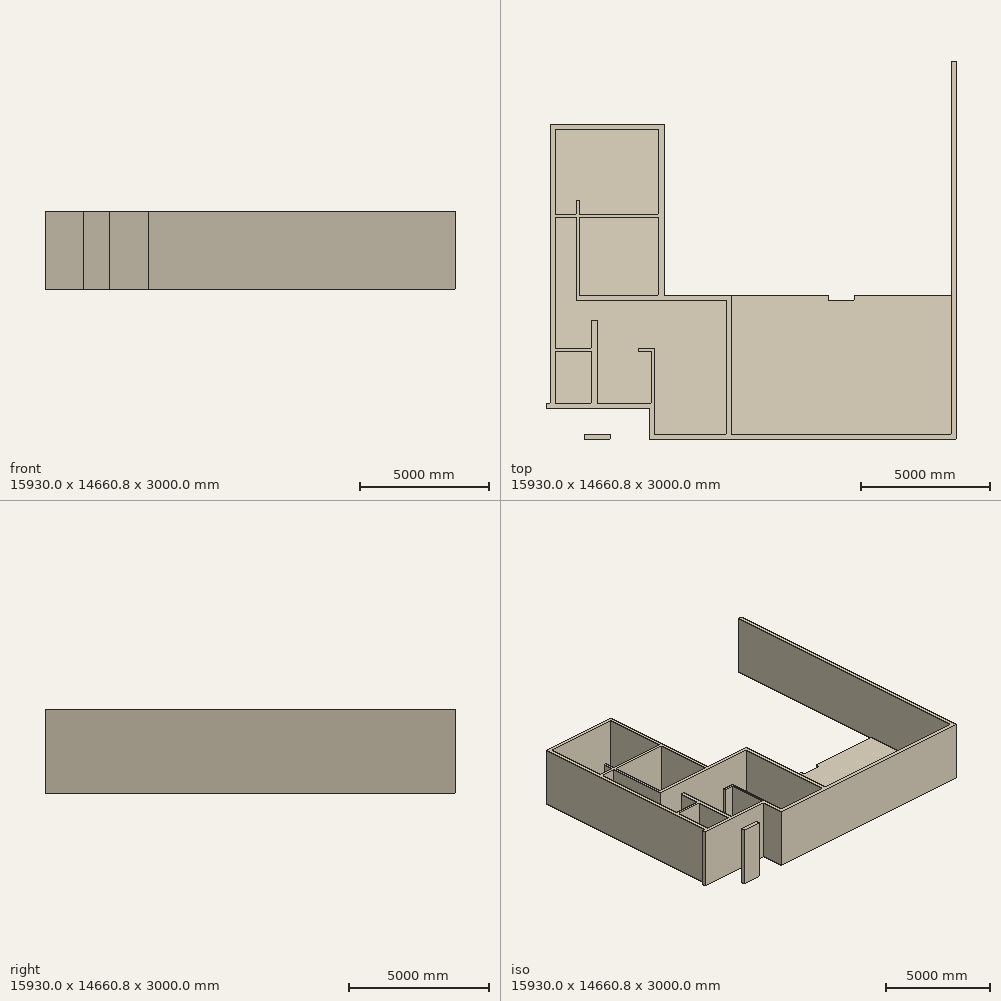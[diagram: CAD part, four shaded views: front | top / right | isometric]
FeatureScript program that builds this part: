
annotation { "Feature Type Name" : "Feature", "Feature Type Description" : "" }
export const myFeature = defineFeature(function(context is Context, id is Id, definition is map)
    precondition{}
    {
        {
            var Q0;
            Q0=qCreatedBy(makeId("Top.planeOp"),FACE);
            var sketch = newSketch(context, id + "F0", { "sketchPlane" : qUnion([Q0])});
            skLineSegment(sketch, "E0.bottom", {"start": v(-7965, 7850) * mm, "end": v(7965, 7850) * mm});
            skLineSegment(sketch, "E0.top", {"start": v(-7965, -7850) * mm, "end": v(7965, -7850) * mm});
            skLineSegment(sketch, "E0.left", {"start": v(-7965, 7850) * mm, "end": v(-7965, -7850) * mm});
            skLineSegment(sketch, "E0.right", {"start": v(7965, 7850) * mm, "end": v(7965, -7850) * mm});
            skSolve(sketch);
        }
        {
            var Q0;
            Q0=qCreatedBy(makeId("Top.planeOp"),FACE);
            var sketch = newSketch(context, id + "F1", { "sketchPlane" : qUnion([Q0])});
            skLineSegment(sketch, "E1", {"start": v(-7797.5, 5409.25) * mm, "end": v(-3397.5, 5409.25) * mm});
            skLineSegment(sketch, "E2", {"start": v(-3397.5, 5409.25) * mm, "end": v(-3397.5, -1210.75) * mm});
            skLineSegment(sketch, "E3", {"start": v(-3397.5, -1210.75) * mm, "end": v(-777.5, -1210.75) * mm});
            skLineSegment(sketch, "E4", {"start": v(-777.5, -1210.75) * mm, "end": v(-777.5, -6610.75) * mm});
            skLineSegment(sketch, "E5", {"start": v(7965, -6810.75) * mm, "end": v(-3977.5, -6810.75) * mm});
            skLineSegment(sketch, "E6", {"start": v(-3977.5, -6810.75) * mm, "end": v(-3977.5, -5610.75) * mm});
            skLineSegment(sketch, "E7", {"start": v(-3977.5, -5610.75) * mm, "end": v(-7437.94, -5610.75) * mm});
            skLineSegment(sketch, "E8", {"start": v(-7597.5, 5209.25) * mm, "end": v(-3597.5, 5209.25) * mm});
            skLineSegment(sketch, "E9", {"start": v(-3597.5, 5209.25) * mm, "end": v(-3597.5, 1909.25) * mm});
            skLineSegment(sketch, "E10", {"start": v(-3597.5, 1909.25) * mm, "end": v(-6697.5, 1909.25) * mm});
            skLineSegment(sketch, "E11", {"start": v(-6697.5, 1909.25) * mm, "end": v(-6697.5, 2459.25) * mm});
            skLineSegment(sketch, "E12", {"start": v(-6697.5, 2459.25) * mm, "end": v(-6817.5, 2459.25) * mm});
            skLineSegment(sketch, "E13", {"start": v(-6817.5, 2459.25) * mm, "end": v(-6817.5, 1909.25) * mm});
            skLineSegment(sketch, "E14", {"start": v(-6817.5, 1909.25) * mm, "end": v(-7597.5, 1909.25) * mm});
            skLineSegment(sketch, "E15", {"start": v(-7597.5, 1909.25) * mm, "end": v(-7597.5, 5209.25) * mm});
            skLineSegment(sketch, "E16.bottom", {"start": v(-6697.5, 1789.25) * mm, "end": v(-3597.5, 1789.25) * mm});
            skLineSegment(sketch, "E16.top", {"start": v(-6697.5, -1210.75) * mm, "end": v(-3597.5, -1210.75) * mm});
            skLineSegment(sketch, "E16.left", {"start": v(-6697.5, 1789.25) * mm, "end": v(-6697.5, -1210.75) * mm});
            skLineSegment(sketch, "E16.right", {"start": v(-3597.5, 1789.25) * mm, "end": v(-3597.5, -1210.75) * mm});
            skLineSegment(sketch, "E17", {"start": v(-7597.5, 1789.25) * mm, "end": v(-6817.5, 1789.25) * mm});
            skLineSegment(sketch, "E18", {"start": v(-6817.5, 1789.25) * mm, "end": v(-6817.5, -1410.75) * mm});
            skLineSegment(sketch, "E19", {"start": v(-6817.5, -1410.75) * mm, "end": v(-977.5, -1410.75) * mm});
            skLineSegment(sketch, "E20", {"start": v(-977.5, -1410.75) * mm, "end": v(-977.5, -6610.75) * mm});
            skLineSegment(sketch, "E21", {"start": v(-977.5, -6610.75) * mm, "end": v(-3777.5, -6610.75) * mm});
            skLineSegment(sketch, "E22", {"start": v(-3777.5, -6610.75) * mm, "end": v(-3777.5, -3290.75) * mm});
            skLineSegment(sketch, "E23", {"start": v(-3777.5, -3290.75) * mm, "end": v(-4397.5, -3290.75) * mm});
            skLineSegment(sketch, "E24", {"start": v(-4397.5, -3290.75) * mm, "end": v(-4397.5, -3410.75) * mm});
            skLineSegment(sketch, "E25", {"start": v(-4397.5, -3410.75) * mm, "end": v(-3897.5, -3410.75) * mm});
            skLineSegment(sketch, "E26", {"start": v(-3897.5, -3410.75) * mm, "end": v(-3897.5, -5410.75) * mm});
            skLineSegment(sketch, "E27", {"start": v(-3897.5, -5410.75) * mm, "end": v(-5997.5, -5410.75) * mm});
            skLineSegment(sketch, "E28", {"start": v(-5997.5, -5410.75) * mm, "end": v(-5997.5, -2190.75) * mm});
            skLineSegment(sketch, "E29", {"start": v(-5997.5, -2190.75) * mm, "end": v(-6197.5, -2190.75) * mm});
            skLineSegment(sketch, "E30", {"start": v(-6197.5, -2190.75) * mm, "end": v(-6197.5, -3290.75) * mm});
            skLineSegment(sketch, "E31", {"start": v(-6197.5, -3290.75) * mm, "end": v(-7597.5, -3290.75) * mm});
            skLineSegment(sketch, "E32", {"start": v(-7597.5, -3290.75) * mm, "end": v(-7597.5, 1789.25) * mm});
            skLineSegment(sketch, "E33.bottom", {"start": v(-7597.5, -3410.75) * mm, "end": v(-6197.5, -3410.75) * mm});
            skLineSegment(sketch, "E33.top", {"start": v(-7597.5, -5410.75) * mm, "end": v(-6197.5, -5410.75) * mm});
            skLineSegment(sketch, "E33.left", {"start": v(-7597.5, -3410.75) * mm, "end": v(-7597.5, -5410.75) * mm});
            skLineSegment(sketch, "E33.right", {"start": v(-6197.5, -3410.75) * mm, "end": v(-6197.5, -5410.75) * mm});
            skLineSegment(sketch, "E34", {"start": v(-3597.5, 5409.25) * mm, "end": v(-3597.5, 5209.25) * mm, "construction": true});
            skLineSegment(sketch, "E35", {"start": v(-3397.5, 5209.25) * mm, "end": v(-3597.5, 5209.25) * mm, "construction": true});
            skLineSegment(sketch, "E36", {"start": v(-7797.5, 5209.25) * mm, "end": v(-7597.5, 5209.25) * mm, "construction": true});
            skLineSegment(sketch, "E37", {"start": v(-6697.5, 1909.25) * mm, "end": v(-6697.5, 1789.25) * mm, "construction": true});
            skLineSegment(sketch, "E38", {"start": v(-3397.5, -1210.75) * mm, "end": v(-3397.5, -1410.75) * mm, "construction": true});
            skLineSegment(sketch, "E39", {"start": v(-977.5, -1410.75) * mm, "end": v(-777.5, -1410.75) * mm, "construction": true});
            skLineSegment(sketch, "E40", {"start": v(-3777.5, -6610.75) * mm, "end": v(-3777.5, -6810.75) * mm, "construction": true});
            skLineSegment(sketch, "E41", {"start": v(-6197.5, -3290.75) * mm, "end": v(-6197.5, -3410.75) * mm, "construction": true});
            skLineSegment(sketch, "E42", {"start": v(-3777.5, -5610.75) * mm, "end": v(-3977.5, -5610.75) * mm, "construction": true});
            skLineSegment(sketch, "E43", {"start": v(-3897.5, -5410.75) * mm, "end": v(-3777.5, -5410.75) * mm, "construction": true});
            skLineSegment(sketch, "E44.bottom", {"start": v(-6477.5, -6610.75) * mm, "end": v(-5477.5, -6610.75) * mm});
            skLineSegment(sketch, "E44.top", {"start": v(-6477.5, -6810.75) * mm, "end": v(-5477.5, -6810.75) * mm});
            skLineSegment(sketch, "E44.left", {"start": v(-6477.5, -6610.75) * mm, "end": v(-6477.5, -6810.75) * mm});
            skLineSegment(sketch, "E44.right", {"start": v(-5477.5, -6610.75) * mm, "end": v(-5477.5, -6810.75) * mm});
            skLineSegment(sketch, "E45", {"start": v(-6197.5, -5610.75) * mm, "end": v(-6197.5, -5410.75) * mm, "construction": true});
            skLineSegment(sketch, "E46", {"start": v(-6197.5, -2190.75) * mm, "end": v(-6197.5, -1410.75) * mm, "construction": true});
            skLineSegment(sketch, "E47", {"start": v(7965, -6810.75) * mm, "end": v(7965, 7850) * mm});
            skLineSegment(sketch, "E48", {"start": v(7965, 7850) * mm, "end": v(7765, 7850) * mm});
            skLineSegment(sketch, "E49", {"start": v(7765, 7850) * mm, "end": v(7765, -6610.75) * mm});
            skLineSegment(sketch, "E50", {"start": v(7765, -6610.75) * mm, "end": v(-777.5, -6610.75) * mm});
            skLineSegment(sketch, "E51", {"start": v(-7437.94, -5610.75) * mm, "end": v(-7965, -5610.75) * mm});
            skLineSegment(sketch, "E52", {"start": v(-7965, -5610.75) * mm, "end": v(-7965, -5410.75) * mm});
            skLineSegment(sketch, "E53", {"start": v(-7965, -5410.75) * mm, "end": v(-7797.5, -5410.75) * mm});
            skLineSegment(sketch, "E54", {"start": v(-7797.5, -5410.75) * mm, "end": v(-7797.5, 5409.25) * mm});
            skLineSegment(sketch, "E55", {"start": v(-777.5, -1210.75) * mm, "end": v(7765, -1210.75) * mm});
            skLineSegment(sketch, "E56.bottom", {"start": v(2993.75, -1210.75) * mm, "end": v(3993.75, -1210.75) * mm});
            skLineSegment(sketch, "E56.top", {"start": v(2993.75, -1410.75) * mm, "end": v(3993.75, -1410.75) * mm});
            skLineSegment(sketch, "E56.left", {"start": v(2993.75, -1210.75) * mm, "end": v(2993.75, -1410.75) * mm});
            skLineSegment(sketch, "E56.right", {"start": v(3993.75, -1210.75) * mm, "end": v(3993.75, -1410.75) * mm});
            skLineSegment(sketch, "E57", {"start": v(3493.75, -1210.75) * mm, "end": v(3493.75, -1410.75) * mm, "construction": true});
            skSolve(sketch);
        }
        {
            var Q0;
            Q0=makeQuery(id+"F1.imprint","IMPRINT",FACE,{"disambiguationData":[TD([[makeQuery(id+"F1.imprint","IMPRINT",EDGE,{"derivedFrom":sQuery(id+"F1.wireOp",EDGE,"E1")}),-1.0]])]});
            var Q1;
            Q1=makeQuery(id+"F1.imprint","IMPRINT",FACE,{"disambiguationData":[TD([[makeQuery(id+"F1.imprint","IMPRINT",EDGE,{"derivedFrom":sQuery(id+"F1.wireOp",EDGE,"E44.bottom")}),-1.0]])]});
            var Q2;
            Q2=makeQuery(id+"F1.imprint","IMPRINT",FACE,{"disambiguationData":[TD([[makeQuery(id+"F1.imprint","IMPRINT",EDGE,{"derivedFrom":sQuery(id+"F1.wireOp",EDGE,"E56.bottom")}),-1.0]])]});
            extrude(context, id + "F2", {"entities" : qUnion([Q0, Q1, Q2]), "depth" : 3000 * mm});
        }
        {
            var Q0;
            Q0=makeQuery(id+"F1.imprint","IMPRINT",FACE,{"disambiguationData":[TD([[makeQuery(id+"F1.imprint","IMPRINT",EDGE,{"derivedFrom":sQuery(id+"F1.wireOp",EDGE,"E8")}),-1.0]])]});
            var Q1;
            Q1=makeQuery(id+"F1.imprint","IMPRINT",FACE,{"disambiguationData":[TD([[makeQuery(id+"F1.imprint","IMPRINT",EDGE,{"derivedFrom":sQuery(id+"F1.wireOp",EDGE,"E16.bottom")}),-1.0]])]});
            var Q2;
            Q2=makeQuery(id+"F1.imprint","IMPRINT",FACE,{"disambiguationData":[TD([[makeQuery(id+"F1.imprint","IMPRINT",EDGE,{"derivedFrom":sQuery(id+"F1.wireOp",EDGE,"E17")}),-1.0]])]});
            var Q3;
            Q3=makeQuery(id+"F1.imprint","IMPRINT",FACE,{"disambiguationData":[TD([[makeQuery(id+"F1.imprint","IMPRINT",EDGE,{"derivedFrom":sQuery(id+"F1.wireOp",EDGE,"E33.bottom")}),-1.0]])]});
            var Q4;
            Q4=makeQuery(id+"F1.imprint","IMPRINT",FACE,{"disambiguationData":[TD([[makeQuery(id+"F1.imprint","IMPRINT",EDGE,{"derivedFrom":sQuery(id+"F1.wireOp",EDGE,"E4")}),1.0]])]});
            extrude(context, id + "F3", {"entities" : qUnion([Q0, Q1, Q2, Q3, Q4]), "depth" : 50 * mm});
        }
    });
